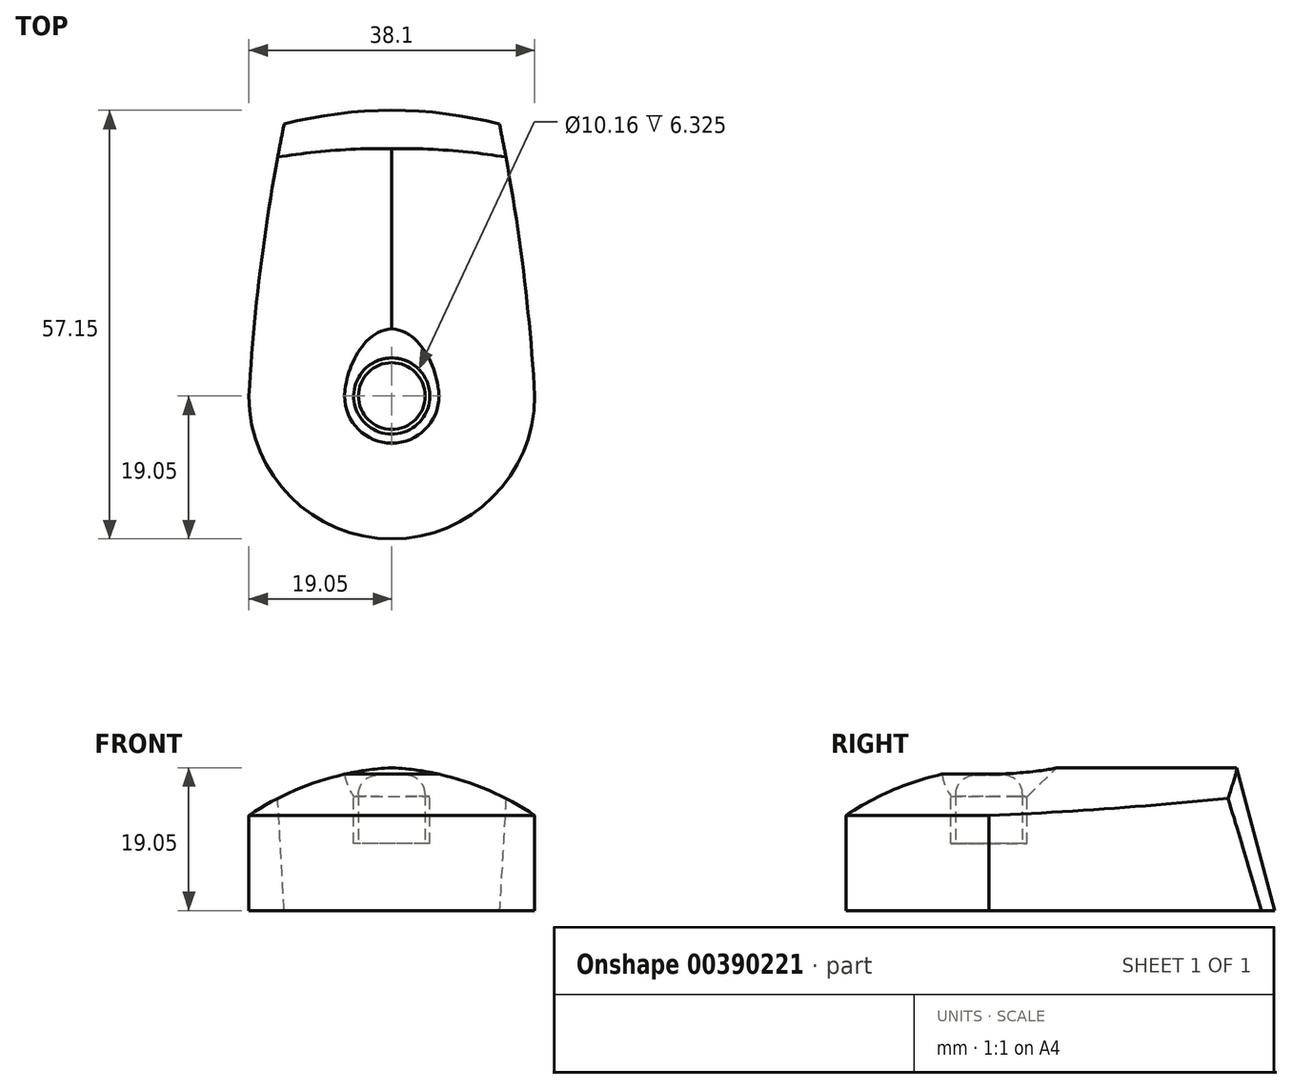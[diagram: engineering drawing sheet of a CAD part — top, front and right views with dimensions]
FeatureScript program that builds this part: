
annotation { "Feature Type Name" : "Feature", "Feature Type Description" : "" }
export const myFeature = defineFeature(function(context is Context, id is Id, definition is map)
    precondition{}
    {
        {
            var Q0;
            Q0=qCreatedBy(makeId("Right.planeOp"),FACE);
            var sketch = newSketch(context, id + "F0", { "sketchPlane" : qUnion([Q0])});
            skLineSegment(sketch, "E0.bottom", {"start": v(0, 0) * mm, "end": v(-19.05, 0) * mm});
            skLineSegment(sketch, "E0.top", {"start": v(0, 12.7) * mm, "end": v(-19.05, 12.7) * mm, "construction": true});
            skLineSegment(sketch, "E0.left", {"start": v(0, 0) * mm, "end": v(0, 12.7) * mm});
            skLineSegment(sketch, "E0.right", {"start": v(-19.05, 0) * mm, "end": v(-19.05, 12.7) * mm});
            skLineSegment(sketch, "E1", {"start": v(0, 12.7) * mm, "end": v(0, 19.05) * mm});
            skArc(sketch, "E2", {"start": v(0, 19.05) * mm, "mid": v(-9.95, 17.15) * mm, "end": v(-19.05, 12.7) * mm});
            skSolve(sketch);
        }
        {
            var Q0;
            Q0=makeQuery(id+"F0.imprint","IMPRINT",FACE,{"disambiguationData":[TD([[makeQuery(id+"F0.imprint","IMPRINT",EDGE,{"derivedFrom":sQuery(id+"F0.wireOp",EDGE,"E0.bottom")}),-1.0]])]});
            var Q1;
            Q1=sQuery(id+"F0.wireOp",EDGE,"E0.left");
            revolve(context, id + "F1", {"entities" : qUnion([Q0]), "axis" : qUnion([Q1]), "revolveType" : RevolveType.SYMMETRIC, "oppositeDirection" : true, "angle" : 180 * degree});
        }
        {
            var Q0;
            Q0=makeQuery(id+"F1.opRevolve","CAP_FACE",FACE,{"disambiguationData":[OSD([sQuery(id+"F0.wireOp",EDGE,"E0.bottom"),sQuery(id+"F0.wireOp",EDGE,"E0.left"),sQuery(id+"F0.wireOp",EDGE,"E0.right"),sQuery(id+"F0.wireOp",EDGE,"E1"),sQuery(id+"F0.wireOp",EDGE,"E2")])],"isStart":false});
            extrude(context, id + "F2", {"entities" : qUnion([Q0]), "operationType" : NewBodyOperationType.ADD, "depth" : 38.1 * mm});
        }
        {
            var Q0;
            {var subQ0=sQuery(id+"F0.wireOp",EDGE,"E0.bottom");Q0=makeQuery(id+"F2.boolean.opBoolean","MERGE",FACE,{"derivedFrom":[makeQuery(id+"F1.opRevolve","SWEPT_FACE",FACE,{"disambiguationData":[OSD([subQ0])]}),makeQuery(id+"F2.opExtrude","SWEPT_FACE",FACE,{"disambiguationData":[OSD([subQ0])]})]});}
            var sketch = newSketch(context, id + "F3", { "sketchPlane" : qUnion([Q0])});
            skLineSegment(sketch, "E3.0", {"start": v(-19.05, -38.1) * mm, "end": v(-19.05, 0) * mm, "construction": true});
            skLineSegment(sketch, "E4.0", {"start": v(19.05, -38.1) * mm, "end": v(19.05, 0) * mm, "construction": true});
            skArc(sketch, "E5.0", {"start": v(-19.05, 0) * mm, "mid": v(0, 19.05) * mm, "end": v(19.05, 0) * mm, "construction": true});
            skLineSegment(sketch, "E6.0", {"start": v(13.97, -38.1) * mm, "end": v(-13.97, -38.1) * mm});
            skLineSegment(sketch, "E7", {"start": v(-19.05, -38.1) * mm, "end": v(-13.97, -38.1) * mm, "construction": true});
            skLineSegment(sketch, "E8", {"start": v(19.05, -38.1) * mm, "end": v(13.97, -38.1) * mm, "construction": true});
            skArc(sketch, "E9", {"start": v(-19.05, 0) * mm, "mid": v(-17.23, -19.15) * mm, "end": v(-13.97, -38.1) * mm});
            skArc(sketch, "E10", {"start": v(13.97, -38.1) * mm, "mid": v(17.23, -19.15) * mm, "end": v(19.05, 0) * mm});
            skSolve(sketch);
        }
        {
            var Q0;
            {var subQ0=sQuery(id+"F3.wireOp",EDGE,"E10");Q0=makeQuery(id+"F3.imprint","IMPRINT",FACE,{"disambiguationData":[TD([[makeQuery(id+"F3.imprint","IMPRINT",EDGE,{"derivedFrom":subQ0}),-1.0]])]});}
            var Q1;
            {var subQ0=sQuery(id+"F3.wireOp",EDGE,"E9");Q1=makeQuery(id+"F3.imprint","IMPRINT",FACE,{"disambiguationData":[TD([[makeQuery(id+"F3.imprint","IMPRINT",EDGE,{"derivedFrom":subQ0}),-1.0]])]});}
            extrude(context, id + "F4", {"entities" : qUnion([Q0, Q1]), "operationType" : NewBodyOperationType.REMOVE, "endBound" : BoundingType.THROUGH_ALL, "oppositeDirection" : true, "depth" : 25.4 * mm});
        }
        {
            var Q0;
            Q0=qCreatedBy(makeId("Right.planeOp"),FACE);
            var sketch = newSketch(context, id + "F5", { "sketchPlane" : qUnion([Q0])});
            skLineSegment(sketch, "E11.0", {"start": v(38.1, 15.55) * mm, "end": v(38.1, 0) * mm});
            skLineSegment(sketch, "E12.0", {"start": v(38.1, 19.05) * mm, "end": v(38.1, 15.55) * mm, "construction": true});
            skLineSegment(sketch, "E13", {"start": v(38.1, 0) * mm, "end": v(33, 19.05) * mm});
            skLineSegment(sketch, "E14", {"start": v(33, 19.05) * mm, "end": v(38.1, 19.05) * mm});
            skLineSegment(sketch, "E15.0.0", {"start": v(0, 12.7) * mm, "end": v(0, 0) * mm});
            skLineSegment(sketch, "E15.0.1", {"start": v(0, 0) * mm, "end": v(38.1, 0) * mm});
            skLineSegment(sketch, "E15.0.2", {"start": v(38.1, 0) * mm, "end": v(38.1, 15.55) * mm, "construction": true});
            skLineSegment(sketch, "E16", {"start": v(-19.05, 0) * mm, "end": v(-19.05, 12.7) * mm});
            skLineSegment(sketch, "E17", {"start": v(38.1, 19.05) * mm, "end": v(45.72, 19.05) * mm});
            skLineSegment(sketch, "E18", {"start": v(45.72, 19.05) * mm, "end": v(45.72, 0) * mm});
            skLineSegment(sketch, "E19", {"start": v(45.72, 0) * mm, "end": v(38.1, 0) * mm});
            skSolve(sketch);
        }
        {
            var Q0;
            Q0=makeQuery(id+"F5.imprint","IMPRINT",FACE,{"disambiguationData":[TD([[makeQuery(id+"F5.imprint","IMPRINT",EDGE,{"derivedFrom":sQuery(id+"F5.wireOp",EDGE,"E13")}),-1.0]])]});
            var Q1;
            Q1=sQuery(id+"F5.wireOp",EDGE,"E16");
            revolve(context, id + "F6", {"operationType" : NewBodyOperationType.REMOVE, "entities" : qUnion([Q0]), "axis" : qUnion([Q1]), "revolveType" : RevolveType.SYMMETRIC, "oppositeDirection" : true, "angle" : 180 * degree});
        }
        {
            var Q0;
            Q0=qCreatedBy(makeId("Right.planeOp"),FACE);
            var sketch = newSketch(context, id + "F7", { "sketchPlane" : qUnion([Q0])});
            skLineSegment(sketch, "E20", {"start": v(4.5, 14.56) * mm, "end": v(19.19, 29.26) * mm});
            skArc(sketch, "E21", {"start": v(-4.5, 14.56) * mm, "mid": v(0, 12.7) * mm, "end": v(4.5, 14.56) * mm});
            skLineSegment(sketch, "E22", {"start": v(-4.5, 14.56) * mm, "end": v(14.7, 33.75) * mm});
            skLineSegment(sketch, "E23", {"start": v(14.7, 33.75) * mm, "end": v(19.19, 29.26) * mm});
            skLineSegment(sketch, "E24", {"start": v(14.7, 33.75) * mm, "end": v(20.38, 39.43) * mm, "construction": true});
            skSolve(sketch);
        }
        {
            var Q0;
            Q0 = qSketchRegion(id + "F7", true);
            var Q1;
            Q1=sQuery(id+"F7.wireOp",EDGE,"E24");
            revolve(context, id + "F8", {"operationType" : NewBodyOperationType.REMOVE, "entities" : qUnion([Q0]), "axis" : qUnion([Q1]), "revolveType" : RevolveType.FULL, "oppositeDirection" : true});
        }
        {
            var Q0;
            Q0=qCreatedBy(makeId("Top.planeOp"),FACE);
            cPlane(context, id + "F9", {"entities" : qUnion([Q0]), "cplaneType" : CPlaneType.OFFSET, "offset" : 15.27 * mm, "width" : 152.4 * mm, "height" : 152.4 * mm});
        }
        {
            var Q0;
            Q0=qCreatedBy(id+"F9.planeOp",FACE);
            var sketch = newSketch(context, id + "F10", { "sketchPlane" : qUnion([Q0])});
            skFitSpline(sketch, "E25.0", {"points": [v(-6.23, 0.86) * mm, v(-6.17, 1.32) * mm, v(-6, 2.22) * mm, v(-5.62, 3.53) * mm, v(-5.18, 4.59) * mm, v(-4.75, 5.4) * mm, v(-4.4, 6) * mm, v(-4, 6.55) * mm, v(-3.57, 7.08) * mm, v(-3.08, 7.57) * mm, v(-2.55, 8.01) * mm, v(-1.98, 8.4) * mm, v(-1.35, 8.7) * mm, v(-0.7, 8.9) * mm, v(-0.23, 8.97) * mm, v(0, 8.98) * mm]});
            skFitSpline(sketch, "E26.0", {"points": [v(6.23, 0.86) * mm, v(6.17, 1.32) * mm, v(6, 2.22) * mm, v(5.62, 3.53) * mm, v(5.18, 4.59) * mm, v(4.75, 5.4) * mm, v(4.4, 6) * mm, v(4, 6.55) * mm, v(3.57, 7.08) * mm, v(3.08, 7.57) * mm, v(2.55, 8.01) * mm, v(1.98, 8.4) * mm, v(1.35, 8.7) * mm, v(0.7, 8.9) * mm, v(0.23, 8.97) * mm, v(0, 8.98) * mm]});
            skArc(sketch, "E27.0", {"start": v(6.29, 0) * mm, "mid": v(0, -6.29) * mm, "end": v(-6.29, 0) * mm});
            skFitSpline(sketch, "E28.0", {"points": [v(-6.29, 0) * mm, v(-6.29, 0.3) * mm, v(-6.27, 0.58) * mm, v(-6.23, 0.86) * mm]});
            skFitSpline(sketch, "E29.0", {"points": [v(6.29, 0) * mm, v(6.29, 0.3) * mm, v(6.27, 0.58) * mm, v(6.23, 0.86) * mm]});
            skLineSegment(sketch, "E30", {"start": v(0, 8.98) * mm, "end": v(0, -6.29) * mm, "construction": true});
            skCircle(sketch, "E31", {"center": v(0, 0) * mm, "radius": 5.08 * mm});
            skCircle(sketch, "E32", {"center": v(0, 0) * mm, "radius": 4.45 * mm});
            skSolve(sketch);
        }
        {
            var Q0;
            Q0=makeQuery(id+"F10.imprint","IMPRINT",FACE,{"disambiguationData":[TD([[makeQuery(id+"F10.imprint","IMPRINT",EDGE,{"derivedFrom":sQuery(id+"F10.wireOp",EDGE,"E31")}),1.0]])]});
            var Q1;
            Q1=makeQuery(id+"F10.imprint","IMPRINT",FACE,{"disambiguationData":[TD([[makeQuery(id+"F10.imprint","IMPRINT",EDGE,{"derivedFrom":sQuery(id+"F10.wireOp",EDGE,"E32")}),1.0]])]});
            extrude(context, id + "F11", {"entities" : qUnion([Q0, Q1]), "operationType" : NewBodyOperationType.REMOVE, "oppositeDirection" : true, "depth" : 6.35 * mm});
        }
        {
            var Q0;
            Q0=makeQuery(id+"F10.imprint","IMPRINT",FACE,{"disambiguationData":[TD([[makeQuery(id+"F10.imprint","IMPRINT",EDGE,{"derivedFrom":sQuery(id+"F10.wireOp",EDGE,"E32")}),1.0]])]});
            extrude(context, id + "F12", {"entities" : qUnion([Q0]), "operationType" : NewBodyOperationType.ADD, "depth" : 2.8 * mm, "hasSecondDirection" : true, "secondDirectionOppositeDirection" : true, "secondDirectionDepth" : 6.35 * mm});
        }
        {
            var Q0;
            Q0=makeQuery(id+"F12.opExtrude","CAP_EDGE",EDGE,{"disambiguationData":[OSD([sQuery(id+"F10.wireOp",EDGE,"E32")])],"isStart":false});
            fillet(context, id + "F13", {"entities" : qUnion([Q0]), "radius" : 2.54 * mm, "tangentPropagation" : true, "allowEdgeOverflow" : false});
        }
    });
